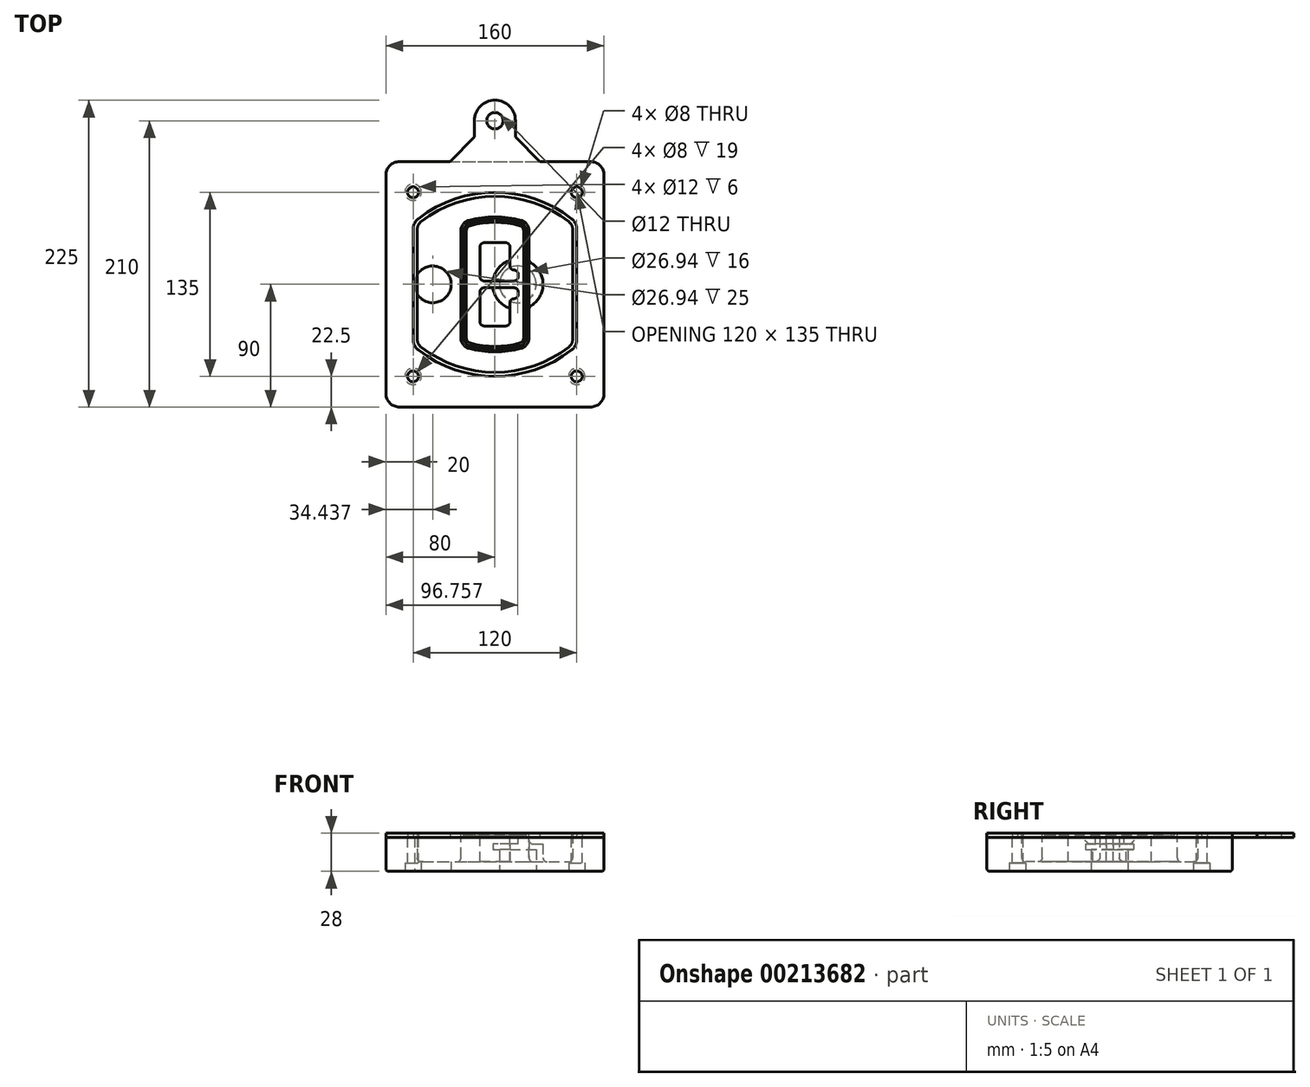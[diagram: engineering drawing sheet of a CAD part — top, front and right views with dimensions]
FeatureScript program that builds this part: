
annotation { "Feature Type Name" : "Feature", "Feature Type Description" : "" }
export const myFeature = defineFeature(function(context is Context, id is Id, definition is map)
    precondition{}
    {
        {
            var Q0;
            Q0=qCreatedBy(makeId("Top.planeOp"),FACE);
            var sketch = newSketch(context, id + "F0", { "sketchPlane" : qUnion([Q0])});
            skPoint(sketch, "E0.rect.middle", {"position": v(0, 0) * mm});
            skLineSegment(sketch, "E1.bottom", {"start": v(-70, -90) * mm, "end": v(70, -90) * mm});
            skLineSegment(sketch, "E1.top", {"start": v(-70, 90) * mm, "end": v(70, 90) * mm});
            skLineSegment(sketch, "E1.left", {"start": v(-80, -80) * mm, "end": v(-80, 80) * mm});
            skLineSegment(sketch, "E1.right", {"start": v(80, -80) * mm, "end": v(80, 80) * mm});
            skLineSegment(sketch, "E2", {"start": v(-80, 90) * mm, "end": v(80, -90) * mm, "construction": true});
            skLineSegment(sketch, "E3", {"start": v(80, 90) * mm, "end": v(-80, -90) * mm, "construction": true});
            skCircle(sketch, "E4", {"center": v(-60, 67.5) * mm, "radius": 4 * mm});
            skCircle(sketch, "E5", {"center": v(60, 67.5) * mm, "radius": 4 * mm});
            skCircle(sketch, "E6", {"center": v(60, -67.5) * mm, "radius": 4 * mm});
            skCircle(sketch, "E7", {"center": v(-60, -67.5) * mm, "radius": 4 * mm});
            skLineSegment(sketch, "E8", {"start": v(-60, 67.5) * mm, "end": v(60, 67.5) * mm, "construction": true});
            skLineSegment(sketch, "E9", {"start": v(60, 67.5) * mm, "end": v(60, -67.5) * mm, "construction": true});
            skLineSegment(sketch, "E10", {"start": v(60, -67.5) * mm, "end": v(-60, -67.5) * mm, "construction": true});
            skLineSegment(sketch, "E11", {"start": v(-60, -67.5) * mm, "end": v(-60, 67.5) * mm, "construction": true});
            skLineSegment(sketch, "E12", {"start": v(-60, 40.3) * mm, "end": v(-60, -40.3) * mm});
            skLineSegment(sketch, "E13", {"start": v(60, 40.3) * mm, "end": v(60, -40.3) * mm});
            skArc(sketch, "E14", {"start": v(56.15, 48.18) * mm, "mid": v(0, 67.5) * mm, "end": v(-56.15, 48.18) * mm});
            skArc(sketch, "E15", {"start": v(-56.15, -48.18) * mm, "mid": v(0, -67.5) * mm, "end": v(56.15, -48.18) * mm});
            skLineSegment(sketch, "E16", {"start": v(-60, 0) * mm, "end": v(60, 0) * mm, "construction": true});
            skPoint(sketch, "E17.visualSharp", {"position": v(-60, -45) * mm});
            skArc(sketch, "E17.filletArc", {"start": v(-60, -40.3) * mm, "mid": v(-58.99, -44.68) * mm, "end": v(-56.15, -48.18) * mm});
            skPoint(sketch, "E18.visualSharp", {"position": v(-60, 45) * mm});
            skArc(sketch, "E18.filletArc", {"start": v(-56.15, 48.18) * mm, "mid": v(-58.99, 44.68) * mm, "end": v(-60, 40.3) * mm});
            skPoint(sketch, "E19.visualSharp", {"position": v(60, 45) * mm});
            skArc(sketch, "E19.filletArc", {"start": v(60, 40.3) * mm, "mid": v(58.99, 44.68) * mm, "end": v(56.15, 48.18) * mm});
            skPoint(sketch, "E20.visualSharp", {"position": v(60, -45) * mm});
            skArc(sketch, "E20.filletArc", {"start": v(56.15, -48.18) * mm, "mid": v(58.99, -44.68) * mm, "end": v(60, -40.3) * mm});
            skPoint(sketch, "E21.visualSharp", {"position": v(-80, 90) * mm});
            skArc(sketch, "E21.filletArc", {"start": v(-70, 90) * mm, "mid": v(-77.07, 87.07) * mm, "end": v(-80, 80) * mm});
            skPoint(sketch, "E22.visualSharp", {"position": v(80, 90) * mm});
            skArc(sketch, "E22.filletArc", {"start": v(80, 80) * mm, "mid": v(77.07, 87.07) * mm, "end": v(70, 90) * mm});
            skPoint(sketch, "E23.visualSharp", {"position": v(80, -90) * mm});
            skArc(sketch, "E23.filletArc", {"start": v(70, -90) * mm, "mid": v(77.07, -87.07) * mm, "end": v(80, -80) * mm});
            skPoint(sketch, "E24.visualSharp", {"position": v(-80, -90) * mm});
            skArc(sketch, "E24.filletArc", {"start": v(-80, -80) * mm, "mid": v(-77.07, -87.07) * mm, "end": v(-70, -90) * mm});
            skArc(sketch, "E25.0", {"start": v(57, 40.3) * mm, "mid": v(56.3, 43.36) * mm, "end": v(54.3, 45.81) * mm});
            skLineSegment(sketch, "E25.1", {"start": v(57, 40.3) * mm, "end": v(57, -40.3) * mm});
            skArc(sketch, "E25.2", {"start": v(54.3, -45.81) * mm, "mid": v(56.3, -43.36) * mm, "end": v(57, -40.3) * mm});
            skArc(sketch, "E25.3", {"start": v(-54.3, -45.81) * mm, "mid": v(0, -64.5) * mm, "end": v(54.3, -45.81) * mm});
            skArc(sketch, "E25.4", {"start": v(-57, -40.3) * mm, "mid": v(-56.3, -43.36) * mm, "end": v(-54.3, -45.81) * mm});
            skArc(sketch, "E25.5", {"start": v(54.3, 45.81) * mm, "mid": v(0, 64.5) * mm, "end": v(-54.3, 45.81) * mm});
            skLineSegment(sketch, "E25.6", {"start": v(-57, 40.3) * mm, "end": v(-57, -40.3) * mm});
            skArc(sketch, "E25.7", {"start": v(-54.3, 45.81) * mm, "mid": v(-56.3, 43.36) * mm, "end": v(-57, 40.3) * mm});
            skArc(sketch, "E26.0", {"start": v(-58.62, 51.33) * mm, "mid": v(-62.58, 46.43) * mm, "end": v(-64, 40.3) * mm});
            skArc(sketch, "E26.1", {"start": v(58.62, 51.33) * mm, "mid": v(0, 71.5) * mm, "end": v(-58.62, 51.33) * mm});
            skArc(sketch, "E26.2", {"start": v(64, 40.3) * mm, "mid": v(62.58, 46.43) * mm, "end": v(58.62, 51.33) * mm});
            skLineSegment(sketch, "E26.3", {"start": v(64, 40.3) * mm, "end": v(64, -40.3) * mm});
            skArc(sketch, "E26.4", {"start": v(58.62, -51.33) * mm, "mid": v(62.58, -46.43) * mm, "end": v(64, -40.3) * mm});
            skLineSegment(sketch, "E26.5", {"start": v(-64, 40.3) * mm, "end": v(-64, -40.3) * mm});
            skArc(sketch, "E26.6", {"start": v(-58.62, -51.33) * mm, "mid": v(0, -71.5) * mm, "end": v(58.62, -51.33) * mm});
            skArc(sketch, "E26.7", {"start": v(-64, -40.3) * mm, "mid": v(-62.58, -46.43) * mm, "end": v(-58.62, -51.33) * mm});
            skSolve(sketch);
        }
        {
            var Q0;
            Q0=makeQuery(id+"F0.imprint","IMPRINT",FACE,{"disambiguationData":[TD([[makeQuery(id+"F0.imprint","IMPRINT",EDGE,{"derivedFrom":sQuery(id+"F0.wireOp",EDGE,"E1.bottom")}),1.0]])]});
            var Q1;
            Q1=makeQuery(id+"F0.imprint","IMPRINT",FACE,{"disambiguationData":[TD([[makeQuery(id+"F0.imprint","IMPRINT",EDGE,{"derivedFrom":sQuery(id+"F0.wireOp",EDGE,"E12")}),1.0]])]});
            var Q2;
            Q2=makeQuery(id+"F0.imprint","IMPRINT",FACE,{"disambiguationData":[TD([[makeQuery(id+"F0.imprint","IMPRINT",EDGE,{"derivedFrom":sQuery(id+"F0.wireOp",EDGE,"E25.0")}),1.0]])]});
            var Q3;
            Q3=makeQuery(id+"F0.imprint","IMPRINT",FACE,{"disambiguationData":[TD([[makeQuery(id+"F0.imprint","IMPRINT",EDGE,{"derivedFrom":sQuery(id+"F0.wireOp",EDGE,"E12")}),-1.0]])]});
            extrude(context, id + "F1", {"entities" : qUnion([Q0, Q1, Q2, Q3]), "oppositeDirection" : true, "depth" : 25 * mm});
        }
        {
            var Q0;
            Q0=makeQuery(id+"F0.imprint","IMPRINT",FACE,{"disambiguationData":[TD([[makeQuery(id+"F0.imprint","IMPRINT",EDGE,{"derivedFrom":sQuery(id+"F0.wireOp",EDGE,"E12")}),1.0]])]});
            extrude(context, id + "F2", {"entities" : qUnion([Q0]), "operationType" : NewBodyOperationType.ADD, "depth" : 3 * mm});
        }
        {
            var Q0;
            Q0=makeQuery(id+"F0.imprint","IMPRINT",FACE,{"disambiguationData":[TD([[makeQuery(id+"F0.imprint","IMPRINT",EDGE,{"derivedFrom":sQuery(id+"F0.wireOp",EDGE,"E25.0")}),1.0]])]});
            extrude(context, id + "F3", {"entities" : qUnion([Q0]), "operationType" : NewBodyOperationType.REMOVE, "oppositeDirection" : true, "depth" : 18 * mm});
        }
        {
            var Q0;
            Q0=makeQuery(id+"F2.opExtrude","CAP_FACE",FACE,{"disambiguationData":[OSD([sQuery(id+"F0.wireOp",EDGE,"E12"),sQuery(id+"F0.wireOp",EDGE,"E13"),sQuery(id+"F0.wireOp",EDGE,"E14"),sQuery(id+"F0.wireOp",EDGE,"E15"),sQuery(id+"F0.wireOp",EDGE,"E17.filletArc"),sQuery(id+"F0.wireOp",EDGE,"E18.filletArc"),sQuery(id+"F0.wireOp",EDGE,"E19.filletArc"),sQuery(id+"F0.wireOp",EDGE,"E20.filletArc"),sQuery(id+"F0.wireOp",EDGE,"E25.0"),sQuery(id+"F0.wireOp",EDGE,"E25.1"),sQuery(id+"F0.wireOp",EDGE,"E25.2"),sQuery(id+"F0.wireOp",EDGE,"E25.3"),sQuery(id+"F0.wireOp",EDGE,"E25.4"),sQuery(id+"F0.wireOp",EDGE,"E25.5"),sQuery(id+"F0.wireOp",EDGE,"E25.6"),sQuery(id+"F0.wireOp",EDGE,"E25.7")])],"isStart":false});
            var sketch = newSketch(context, id + "F4", { "sketchPlane" : qUnion([Q0])});
            skArc(sketch, "E27.0", {"start": v(-19.08, -46.97) * mm, "mid": v(0, -49.5) * mm, "end": v(19.08, -46.97) * mm});
            skArc(sketch, "E28.0", {"start": v(19.08, 46.97) * mm, "mid": v(0, 49.5) * mm, "end": v(-19.08, 46.97) * mm});
            skLineSegment(sketch, "E29", {"start": v(-25, 39.25) * mm, "end": v(-25, -39.25) * mm});
            skLineSegment(sketch, "E30", {"start": v(25, 39.25) * mm, "end": v(25, -39.25) * mm});
            skLineSegment(sketch, "E31", {"start": v(-25, 45.1) * mm, "end": v(25, 45.1) * mm, "construction": true});
            skLineSegment(sketch, "E32", {"start": v(-25, -45.1) * mm, "end": v(25, -45.1) * mm, "construction": true});
            skPoint(sketch, "E33.visualSharp", {"position": v(-25, 45.1) * mm});
            skArc(sketch, "E33.filletArc", {"start": v(-19.08, 46.97) * mm, "mid": v(-23.35, 44.11) * mm, "end": v(-25, 39.25) * mm});
            skPoint(sketch, "E34.visualSharp", {"position": v(25, 45.1) * mm});
            skArc(sketch, "E34.filletArc", {"start": v(25, 39.25) * mm, "mid": v(23.35, 44.11) * mm, "end": v(19.08, 46.97) * mm});
            skPoint(sketch, "E35.visualSharp", {"position": v(25, -45.1) * mm});
            skArc(sketch, "E35.filletArc", {"start": v(19.08, -46.97) * mm, "mid": v(23.35, -44.11) * mm, "end": v(25, -39.25) * mm});
            skPoint(sketch, "E36.visualSharp", {"position": v(-25, -45.1) * mm});
            skArc(sketch, "E36.filletArc", {"start": v(-25, -39.25) * mm, "mid": v(-23.35, -44.11) * mm, "end": v(-19.08, -46.97) * mm});
            skArc(sketch, "E37.0", {"start": v(54.3, 45.81) * mm, "mid": v(0, 64.5) * mm, "end": v(-54.3, 45.81) * mm});
            skArc(sketch, "E37.1", {"start": v(-54.3, 45.81) * mm, "mid": v(-56.3, 43.36) * mm, "end": v(-57, 40.3) * mm});
            skLineSegment(sketch, "E37.2", {"start": v(-57, 40.3) * mm, "end": v(-57, -40.3) * mm});
            skArc(sketch, "E37.3", {"start": v(-57, -40.3) * mm, "mid": v(-56.3, -43.36) * mm, "end": v(-54.3, -45.81) * mm});
            skArc(sketch, "E37.4", {"start": v(-54.3, -45.81) * mm, "mid": v(0, -64.5) * mm, "end": v(54.3, -45.81) * mm});
            skArc(sketch, "E37.5", {"start": v(54.3, -45.81) * mm, "mid": v(56.3, -43.36) * mm, "end": v(57, -40.3) * mm});
            skLineSegment(sketch, "E37.6", {"start": v(57, 40.3) * mm, "end": v(57, -40.3) * mm});
            skArc(sketch, "E37.7", {"start": v(57, 40.3) * mm, "mid": v(56.3, 43.36) * mm, "end": v(54.3, 45.81) * mm});
            skLineSegment(sketch, "E38.0", {"start": v(23, 39.25) * mm, "end": v(23, -39.25) * mm});
            skArc(sketch, "E38.1", {"start": v(18.56, -45.04) * mm, "mid": v(21.76, -42.9) * mm, "end": v(23, -39.25) * mm});
            skArc(sketch, "E38.2", {"start": v(-18.56, -45.04) * mm, "mid": v(0, -47.5) * mm, "end": v(18.56, -45.04) * mm});
            skArc(sketch, "E38.3", {"start": v(-23, -39.25) * mm, "mid": v(-21.76, -42.9) * mm, "end": v(-18.56, -45.04) * mm});
            skLineSegment(sketch, "E38.4", {"start": v(-23, 39.25) * mm, "end": v(-23, -39.25) * mm});
            skArc(sketch, "E38.5", {"start": v(23, 39.25) * mm, "mid": v(21.76, 42.9) * mm, "end": v(18.56, 45.04) * mm});
            skArc(sketch, "E38.6", {"start": v(-18.56, 45.04) * mm, "mid": v(-21.76, 42.9) * mm, "end": v(-23, 39.25) * mm});
            skArc(sketch, "E38.7", {"start": v(18.56, 45.04) * mm, "mid": v(0, 47.5) * mm, "end": v(-18.56, 45.04) * mm});
            skArc(sketch, "E39.0", {"start": v(21, 39.25) * mm, "mid": v(20.18, 41.68) * mm, "end": v(18.04, 43.1) * mm});
            skLineSegment(sketch, "E39.1", {"start": v(21, 39.25) * mm, "end": v(21, -39.25) * mm});
            skArc(sketch, "E39.2", {"start": v(18.04, -43.1) * mm, "mid": v(20.18, -41.68) * mm, "end": v(21, -39.25) * mm});
            skArc(sketch, "E39.3", {"start": v(-18.04, -43.1) * mm, "mid": v(0, -45.5) * mm, "end": v(18.04, -43.1) * mm});
            skArc(sketch, "E39.4", {"start": v(-21, -39.25) * mm, "mid": v(-20.18, -41.68) * mm, "end": v(-18.04, -43.1) * mm});
            skArc(sketch, "E39.5", {"start": v(18.04, 43.1) * mm, "mid": v(0, 45.5) * mm, "end": v(-18.04, 43.1) * mm});
            skLineSegment(sketch, "E39.6", {"start": v(-21, 39.25) * mm, "end": v(-21, -39.25) * mm});
            skArc(sketch, "E39.7", {"start": v(-18.04, 43.1) * mm, "mid": v(-20.18, 41.68) * mm, "end": v(-21, 39.25) * mm});
            skLineSegment(sketch, "E40", {"start": v(-25, 0) * mm, "end": v(25, 0) * mm, "construction": true});
            skLineSegment(sketch, "E41", {"start": v(-11, 5.5) * mm, "end": v(-11, 27.5) * mm});
            skLineSegment(sketch, "E42", {"start": v(-8, 30.5) * mm, "end": v(8, 30.5) * mm});
            skLineSegment(sketch, "E43", {"start": v(11, 27.5) * mm, "end": v(11, 13.5) * mm});
            skLineSegment(sketch, "E44", {"start": v(14, 10.5) * mm, "end": v(14, 10.5) * mm});
            skLineSegment(sketch, "E45", {"start": v(17, 7.5) * mm, "end": v(17, 5.5) * mm});
            skLineSegment(sketch, "E46", {"start": v(14, 2.5) * mm, "end": v(-8, 2.5) * mm});
            skPoint(sketch, "E47.visualSharp", {"position": v(-11, 30.5) * mm});
            skArc(sketch, "E47.filletArc", {"start": v(-8, 30.5) * mm, "mid": v(-10.12, 29.62) * mm, "end": v(-11, 27.5) * mm});
            skPoint(sketch, "E48.visualSharp", {"position": v(11, 30.5) * mm});
            skArc(sketch, "E48.filletArc", {"start": v(11, 27.5) * mm, "mid": v(10.12, 29.62) * mm, "end": v(8, 30.5) * mm});
            skPoint(sketch, "E49.visualSharp", {"position": v(11, 10.5) * mm});
            skArc(sketch, "E49.filletArc", {"start": v(11, 13.5) * mm, "mid": v(11.88, 11.38) * mm, "end": v(14, 10.5) * mm});
            skPoint(sketch, "E50.visualSharp", {"position": v(17, 10.5) * mm});
            skArc(sketch, "E50.filletArc", {"start": v(17, 7.5) * mm, "mid": v(16.12, 9.62) * mm, "end": v(14, 10.5) * mm});
            skPoint(sketch, "E51.visualSharp", {"position": v(17, 2.5) * mm});
            skArc(sketch, "E51.filletArc", {"start": v(14, 2.5) * mm, "mid": v(16.12, 3.38) * mm, "end": v(17, 5.5) * mm});
            skPoint(sketch, "E52.visualSharp", {"position": v(-11, 2.5) * mm});
            skArc(sketch, "E52.filletArc", {"start": v(-11, 5.5) * mm, "mid": v(-10.12, 3.38) * mm, "end": v(-8, 2.5) * mm});
            skLineSegment(sketch, "E53.0.MirrorCS", {"start": v(14, -2.5) * mm, "end": v(-8, -2.5) * mm});
            skArc(sketch, "E54.0.MirrorCS", {"start": v(-11, -5.5) * mm, "mid": v(-10.12, -3.38) * mm, "end": v(-8, -2.5) * mm});
            skLineSegment(sketch, "E55.0.MirrorCS", {"start": v(-11, -5.5) * mm, "end": v(-11, -27.5) * mm});
            skArc(sketch, "E56.0.MirrorCS", {"start": v(-8, -30.5) * mm, "mid": v(-10.12, -29.62) * mm, "end": v(-11, -27.5) * mm});
            skLineSegment(sketch, "E57.0.MirrorCS", {"start": v(-8, -30.5) * mm, "end": v(8, -30.5) * mm});
            skArc(sketch, "E58.0.MirrorCS", {"start": v(11, -27.5) * mm, "mid": v(10.12, -29.62) * mm, "end": v(8, -30.5) * mm});
            skLineSegment(sketch, "E59.0.MirrorCS", {"start": v(11, -27.5) * mm, "end": v(11, -13.5) * mm});
            skArc(sketch, "E60.0.MirrorCS", {"start": v(11, -13.5) * mm, "mid": v(11.88, -11.38) * mm, "end": v(14, -10.5) * mm});
            skArc(sketch, "E61.0.MirrorCS", {"start": v(17, -7.5) * mm, "mid": v(16.12, -9.62) * mm, "end": v(14, -10.5) * mm});
            skLineSegment(sketch, "E62.0.MirrorCS", {"start": v(17, -7.5) * mm, "end": v(17, -5.5) * mm});
            skArc(sketch, "E63.0.MirrorCS", {"start": v(14, -2.5) * mm, "mid": v(16.12, -3.38) * mm, "end": v(17, -5.5) * mm});
            skSolve(sketch);
        }
        {
            var Q0;
            Q0=makeQuery(id+"F4.imprint","IMPRINT",FACE,{"disambiguationData":[TD([[makeQuery(id+"F4.imprint","IMPRINT",EDGE,{"derivedFrom":sQuery(id+"F4.wireOp",EDGE,"E27.0")}),1.0]])]});
            var Q1;
            Q1=makeQuery(id+"F4.imprint","IMPRINT",FACE,{"disambiguationData":[TD([[makeQuery(id+"F4.imprint","IMPRINT",EDGE,{"derivedFrom":sQuery(id+"F4.wireOp",EDGE,"E38.0")}),-1.0]])]});
            var Q2;
            Q2=makeQuery(id+"F4.imprint","IMPRINT",FACE,{"disambiguationData":[TD([[makeQuery(id+"F4.imprint","IMPRINT",EDGE,{"derivedFrom":sQuery(id+"F4.wireOp",EDGE,"E39.0")}),1.0]])]});
            extrude(context, id + "F5", {"entities" : qUnion([Q0, Q1, Q2]), "operationType" : NewBodyOperationType.ADD, "endBound" : BoundingType.UP_TO_NEXT, "oppositeDirection" : true, "depth" : 25 * mm});
        }
        {
            var Q0;
            Q0=makeQuery(id+"F4.imprint","IMPRINT",FACE,{"disambiguationData":[TD([[makeQuery(id+"F4.imprint","IMPRINT",EDGE,{"derivedFrom":sQuery(id+"F4.wireOp",EDGE,"E38.0")}),-1.0]])]});
            extrude(context, id + "F6", {"entities" : qUnion([Q0]), "operationType" : NewBodyOperationType.REMOVE, "oppositeDirection" : true, "depth" : 2 * mm});
        }
        {
            var Q0;
            Q0=makeQuery(id+"F1.opExtrude","CAP_FACE",FACE,{"disambiguationData":[OSD([sQuery(id+"F0.wireOp",EDGE,"E1.bottom"),sQuery(id+"F0.wireOp",EDGE,"E1.top"),sQuery(id+"F0.wireOp",EDGE,"E1.left"),sQuery(id+"F0.wireOp",EDGE,"E1.right"),sQuery(id+"F0.wireOp",EDGE,"E4"),sQuery(id+"F0.wireOp",EDGE,"E5"),sQuery(id+"F0.wireOp",EDGE,"E6"),sQuery(id+"F0.wireOp",EDGE,"E7"),sQuery(id+"F0.wireOp",EDGE,"E21.filletArc"),sQuery(id+"F0.wireOp",EDGE,"E22.filletArc"),sQuery(id+"F0.wireOp",EDGE,"E23.filletArc"),sQuery(id+"F0.wireOp",EDGE,"E24.filletArc")])],"isStart":false});
            var sketch = newSketch(context, id + "F7", { "sketchPlane" : qUnion([Q0])});
            skCircle(sketch, "E64", {"center": v(16.76, 0) * mm, "radius": 13.47 * mm});
            skCircle(sketch, "E65", {"center": v(-45.56, 0) * mm, "radius": 13.47 * mm});
            skLineSegment(sketch, "E66", {"start": v(80, 0) * mm, "end": v(-80, 0) * mm});
            skCircle(sketch, "E67", {"center": v(16.76, 0) * mm, "radius": 18.47 * mm});
            skCircle(sketch, "E68", {"center": v(60, -67.5) * mm, "radius": 6 * mm});
            skCircle(sketch, "E69", {"center": v(-60, -67.5) * mm, "radius": 6 * mm});
            skCircle(sketch, "E70", {"center": v(-60, 67.5) * mm, "radius": 6 * mm});
            skCircle(sketch, "E71", {"center": v(60, 67.5) * mm, "radius": 6 * mm});
            skSolve(sketch);
        }
        {
            var Q0;
            {var subQ1=sQuery(id+"F7.wireOp",EDGE,"E66");var subQ4=sQuery(id+"F7.wireOp",EDGE,"E64");var subQ6=makeQuery(id+"F7.imprint","INTERSECT",VERTEX,{"disambiguationData":[OD(0.0)],"derivedFrom":[subQ4,subQ1]});Q0=makeQuery(id+"F7.imprint","IMPRINT",FACE,{"disambiguationData":[TD([[makeQuery(id+"F7.imprint","IMPRINT",EDGE,{"disambiguationData":[TD([[subQ6,-1.0]])],"derivedFrom":subQ4}),-1.0]])]});}
            var Q1;
            {var subQ0=sQuery(id+"F7.wireOp",EDGE,"E66");var subQ1=sQuery(id+"F7.wireOp",EDGE,"E64");var subQ3=makeQuery(id+"F7.imprint","INTERSECT",VERTEX,{"disambiguationData":[OD(0.0)],"derivedFrom":[subQ1,subQ0]});Q1=makeQuery(id+"F7.imprint","IMPRINT",FACE,{"disambiguationData":[TD([[makeQuery(id+"F7.imprint","IMPRINT",EDGE,{"disambiguationData":[TD([[subQ3,-1.0]])],"derivedFrom":subQ1}),1.0]])]});}
            var Q2;
            {var subQ0=sQuery(id+"F7.wireOp",EDGE,"E66");var subQ1=sQuery(id+"F7.wireOp",EDGE,"E64");var subQ3=makeQuery(id+"F7.imprint","INTERSECT",VERTEX,{"disambiguationData":[OD(0.0)],"derivedFrom":[subQ1,subQ0]});Q2=makeQuery(id+"F7.imprint","IMPRINT",FACE,{"disambiguationData":[TD([[makeQuery(id+"F7.imprint","IMPRINT",EDGE,{"disambiguationData":[TD([[subQ3,1.0]])],"derivedFrom":subQ1}),1.0]])]});}
            var Q3;
            {var subQ1=sQuery(id+"F7.wireOp",EDGE,"E66");var subQ4=sQuery(id+"F7.wireOp",EDGE,"E64");var subQ6=makeQuery(id+"F7.imprint","INTERSECT",VERTEX,{"disambiguationData":[OD(0.0)],"derivedFrom":[subQ4,subQ1]});Q3=makeQuery(id+"F7.imprint","IMPRINT",FACE,{"disambiguationData":[TD([[makeQuery(id+"F7.imprint","IMPRINT",EDGE,{"disambiguationData":[TD([[subQ6,1.0]])],"derivedFrom":subQ4}),-1.0]])]});}
            extrude(context, id + "F8", {"entities" : qUnion([Q0, Q1, Q2, Q3]), "operationType" : NewBodyOperationType.ADD, "oppositeDirection" : true, "depth" : 20 * mm});
        }
        {
            var Q0;
            {var subQ0=sQuery(id+"F7.wireOp",EDGE,"E66");var subQ1=sQuery(id+"F7.wireOp",EDGE,"E64");var subQ3=makeQuery(id+"F7.imprint","INTERSECT",VERTEX,{"disambiguationData":[OD(0.0)],"derivedFrom":[subQ1,subQ0]});Q0=makeQuery(id+"F7.imprint","IMPRINT",FACE,{"disambiguationData":[TD([[makeQuery(id+"F7.imprint","IMPRINT",EDGE,{"disambiguationData":[TD([[subQ3,-1.0]])],"derivedFrom":subQ1}),1.0]])]});}
            var Q1;
            {var subQ0=sQuery(id+"F7.wireOp",EDGE,"E66");var subQ1=sQuery(id+"F7.wireOp",EDGE,"E64");var subQ3=makeQuery(id+"F7.imprint","INTERSECT",VERTEX,{"disambiguationData":[OD(0.0)],"derivedFrom":[subQ1,subQ0]});Q1=makeQuery(id+"F7.imprint","IMPRINT",FACE,{"disambiguationData":[TD([[makeQuery(id+"F7.imprint","IMPRINT",EDGE,{"disambiguationData":[TD([[subQ3,1.0]])],"derivedFrom":subQ1}),1.0]])]});}
            extrude(context, id + "F9", {"entities" : qUnion([Q0, Q1]), "operationType" : NewBodyOperationType.REMOVE, "oppositeDirection" : true, "depth" : 16 * mm});
        }
        {
            var Q0;
            {var subQ0=sQuery(id+"F7.wireOp",EDGE,"E66");var subQ1=sQuery(id+"F7.wireOp",EDGE,"E65");var subQ3=makeQuery(id+"F7.imprint","INTERSECT",VERTEX,{"disambiguationData":[OD(0.0)],"derivedFrom":[subQ1,subQ0]});Q0=makeQuery(id+"F7.imprint","IMPRINT",FACE,{"disambiguationData":[TD([[makeQuery(id+"F7.imprint","IMPRINT",EDGE,{"disambiguationData":[TD([[subQ3,-1.0]])],"derivedFrom":subQ1}),1.0]])]});}
            var Q1;
            {var subQ0=sQuery(id+"F7.wireOp",EDGE,"E66");var subQ1=sQuery(id+"F7.wireOp",EDGE,"E65");var subQ3=makeQuery(id+"F7.imprint","INTERSECT",VERTEX,{"disambiguationData":[OD(0.0)],"derivedFrom":[subQ1,subQ0]});Q1=makeQuery(id+"F7.imprint","IMPRINT",FACE,{"disambiguationData":[TD([[makeQuery(id+"F7.imprint","IMPRINT",EDGE,{"disambiguationData":[TD([[subQ3,1.0]])],"derivedFrom":subQ1}),1.0]])]});}
            extrude(context, id + "F10", {"entities" : qUnion([Q0, Q1]), "operationType" : NewBodyOperationType.REMOVE, "oppositeDirection" : true, "depth" : 25 * mm});
        }
        {
            var Q0;
            Q0=makeQuery(id+"F7.imprint","IMPRINT",FACE,{"disambiguationData":[TD([[makeQuery(id+"F7.imprint","IMPRINT",EDGE,{"derivedFrom":sQuery(id+"F7.wireOp",EDGE,"E68")}),1.0]])]});
            var Q1;
            Q1=makeQuery(id+"F7.imprint","IMPRINT",FACE,{"disambiguationData":[TD([[makeQuery(id+"F7.imprint","IMPRINT",EDGE,{"derivedFrom":makeQuery(id+"F1.opExtrude","CAP_EDGE",EDGE,{"disambiguationData":[OSD([sQuery(id+"F0.wireOp",EDGE,"E5")])],"isStart":false})}),-1.0]])]});
            var Q2;
            Q2=makeQuery(id+"F7.imprint","IMPRINT",FACE,{"disambiguationData":[TD([[makeQuery(id+"F7.imprint","IMPRINT",EDGE,{"derivedFrom":sQuery(id+"F7.wireOp",EDGE,"E69")}),1.0]])]});
            var Q3;
            Q3=makeQuery(id+"F7.imprint","IMPRINT",FACE,{"disambiguationData":[TD([[makeQuery(id+"F7.imprint","IMPRINT",EDGE,{"derivedFrom":makeQuery(id+"F1.opExtrude","CAP_EDGE",EDGE,{"disambiguationData":[OSD([sQuery(id+"F0.wireOp",EDGE,"E4")])],"isStart":false})}),-1.0]])]});
            var Q4;
            Q4=makeQuery(id+"F7.imprint","IMPRINT",FACE,{"disambiguationData":[TD([[makeQuery(id+"F7.imprint","IMPRINT",EDGE,{"derivedFrom":sQuery(id+"F7.wireOp",EDGE,"E70")}),1.0]])]});
            var Q5;
            Q5=makeQuery(id+"F7.imprint","IMPRINT",FACE,{"disambiguationData":[TD([[makeQuery(id+"F7.imprint","IMPRINT",EDGE,{"derivedFrom":makeQuery(id+"F1.opExtrude","CAP_EDGE",EDGE,{"disambiguationData":[OSD([sQuery(id+"F0.wireOp",EDGE,"E7")])],"isStart":false})}),-1.0]])]});
            var Q6;
            Q6=makeQuery(id+"F7.imprint","IMPRINT",FACE,{"disambiguationData":[TD([[makeQuery(id+"F7.imprint","IMPRINT",EDGE,{"derivedFrom":sQuery(id+"F7.wireOp",EDGE,"E71")}),1.0]])]});
            var Q7;
            Q7=makeQuery(id+"F7.imprint","IMPRINT",FACE,{"disambiguationData":[TD([[makeQuery(id+"F7.imprint","IMPRINT",EDGE,{"derivedFrom":makeQuery(id+"F1.opExtrude","CAP_EDGE",EDGE,{"disambiguationData":[OSD([sQuery(id+"F0.wireOp",EDGE,"E6")])],"isStart":false})}),-1.0]])]});
            extrude(context, id + "F11", {"entities" : qUnion([Q0, Q1, Q2, Q3, Q4, Q5, Q6, Q7]), "operationType" : NewBodyOperationType.REMOVE, "oppositeDirection" : true, "depth" : 6 * mm});
        }
        {
            var Q0;
            Q0=makeQuery(id+"F9.boolean.opBoolean","COPY",FACE,{"derivedFrom":makeQuery(id+"F9.opExtrude","CAP_FACE",FACE,{"disambiguationData":[OSD([sQuery(id+"F7.wireOp",EDGE,"E64")])],"isStart":false})});
            var sketch = newSketch(context, id + "F12", { "sketchPlane" : qUnion([Q0])});
            skArc(sketch, "E72.0", {"start": v(11, 17.55) * mm, "mid": v(2.57, 11.82) * mm, "end": v(-1.54, 2.5) * mm});
            skArc(sketch, "E72.1", {"start": v(-1.54, -2.5) * mm, "mid": v(2.57, -11.82) * mm, "end": v(11, -17.55) * mm});
            skLineSegment(sketch, "E73", {"start": v(-1.54, -2.5) * mm, "end": v(14, -2.5) * mm});
            skLineSegment(sketch, "E74.0", {"start": v(14, 2.5) * mm, "end": v(-1.54, 2.5) * mm});
            skArc(sketch, "E74.1", {"start": v(14, 2.5) * mm, "mid": v(16.12, 3.38) * mm, "end": v(17, 5.5) * mm});
            skLineSegment(sketch, "E74.2", {"start": v(17, 7.5) * mm, "end": v(17, 5.5) * mm});
            skArc(sketch, "E74.3", {"start": v(17, 7.5) * mm, "mid": v(16.12, 9.62) * mm, "end": v(14, 10.5) * mm});
            skArc(sketch, "E74.4", {"start": v(11, 13.5) * mm, "mid": v(11.88, 11.38) * mm, "end": v(14, 10.5) * mm});
            skLineSegment(sketch, "E74.5", {"start": v(11, 17.55) * mm, "end": v(11, 13.5) * mm});
            skLineSegment(sketch, "E74.7", {"start": v(14, -2.5) * mm, "end": v(-1.54, -2.5) * mm});
            skArc(sketch, "E74.8", {"start": v(14, -2.5) * mm, "mid": v(16.12, -3.38) * mm, "end": v(17, -5.5) * mm});
            skLineSegment(sketch, "E74.9", {"start": v(17, -7.5) * mm, "end": v(17, -5.5) * mm});
            skArc(sketch, "E74.10", {"start": v(17, -7.5) * mm, "mid": v(16.12, -9.62) * mm, "end": v(14, -10.5) * mm});
            skArc(sketch, "E74.11", {"start": v(11, -13.5) * mm, "mid": v(11.88, -11.38) * mm, "end": v(14, -10.5) * mm});
            skLineSegment(sketch, "E74.12", {"start": v(11, -17.55) * mm, "end": v(11, -13.5) * mm});
            skPoint(sketch, "E75.orphan", {"position": v(11, -27.5) * mm});
            skPoint(sketch, "E76.orphan", {"position": v(-8, -2.5) * mm});
            skPoint(sketch, "E77.orphan", {"position": v(-8, 2.5) * mm});
            skPoint(sketch, "E78.orphan", {"position": v(11, 27.5) * mm});
            skSolve(sketch);
        }
        {
            var Q0;
            {var subQ7=sQuery(id+"F12.wireOp",EDGE,"E72.0");var subQ14=sQuery(id+"F12.wireOp",EDGE,"E72.1");var subQ16=sQuery(id+"F12.wireOp",EDGE,"E74.1");var subQ18=sQuery(id+"F12.wireOp",EDGE,"E74.8");Q0=qUnion([makeQuery(id+"F12.imprint","IMPRINT",FACE,{"disambiguationData":[TD([[makeQuery(id+"F12.imprint","IMPRINT",EDGE,{"derivedFrom":subQ7}),1.0]])]}),makeQuery(id+"F12.imprint","IMPRINT",FACE,{"disambiguationData":[TD([[makeQuery(id+"F12.imprint","IMPRINT",EDGE,{"derivedFrom":subQ14}),1.0]])]}),makeQuery(id+"F12.imprint","IMPRINT",FACE,{"disambiguationData":[TD([[makeQuery(id+"F12.imprint","IMPRINT",EDGE,{"derivedFrom":subQ16}),1.0]])]}),makeQuery(id+"F12.imprint","IMPRINT",FACE,{"disambiguationData":[TD([[makeQuery(id+"F12.imprint","IMPRINT",EDGE,{"derivedFrom":subQ18}),-1.0]])]})]);}
            var Q1;
            Q1=makeQuery(id+"F5.boolean.opBoolean","SPLIT",FACE,{"disambiguationData":[TD([makeQuery(id+"F5.opExtrude","SWEPT_FACE",FACE,{"disambiguationData":[OSD([sQuery(id+"F4.wireOp",EDGE,"E41")])]})])],"derivedFrom":makeQuery(id+"F3.boolean.opBoolean","COPY",FACE,{"derivedFrom":makeQuery(id+"F3.opExtrude","CAP_FACE",FACE,{"disambiguationData":[OSD([sQuery(id+"F0.wireOp",EDGE,"E25.0"),sQuery(id+"F0.wireOp",EDGE,"E25.1"),sQuery(id+"F0.wireOp",EDGE,"E25.2"),sQuery(id+"F0.wireOp",EDGE,"E25.3"),sQuery(id+"F0.wireOp",EDGE,"E25.4"),sQuery(id+"F0.wireOp",EDGE,"E25.5"),sQuery(id+"F0.wireOp",EDGE,"E25.6"),sQuery(id+"F0.wireOp",EDGE,"E25.7")])],"isStart":false})})});
            extrude(context, id + "F13", {"entities" : qUnion([Q0]), "operationType" : NewBodyOperationType.REMOVE, "endBound" : BoundingType.UP_TO_SURFACE, "endBoundEntityFace" : qUnion([Q1]), "depth" : 25 * mm});
        }
        {
            var Q0;
            Q0=makeQuery(id+"F3.boolean.opBoolean","COPY",EDGE,{"derivedFrom":makeQuery(id+"F3.opExtrude","CAP_EDGE",EDGE,{"disambiguationData":[OSD([sQuery(id+"F0.wireOp",EDGE,"E25.6")])],"isStart":false})});
            var Q1;
            Q1=makeQuery(id+"F8.boolean.opBoolean","INTERSECT",EDGE,{"derivedFrom":[makeQuery(id+"F5.opExtrude","SWEPT_FACE",FACE,{"disambiguationData":[OSD([sQuery(id+"F4.wireOp",EDGE,"E30")])]}),makeQuery(id+"F8.opExtrude","CAP_FACE",FACE,{"disambiguationData":[OSD([sQuery(id+"F7.wireOp",EDGE,"E67")])],"isStart":false})]});
            var Q2;
            Q2=makeQuery(id+"F8.boolean.opBoolean","INTERSECT",EDGE,{"disambiguationData":[OD(1.0)],"derivedFrom":[makeQuery(id+"F5.opExtrude","SWEPT_FACE",FACE,{"disambiguationData":[OSD([sQuery(id+"F4.wireOp",EDGE,"E30")])]}),makeQuery(id+"F8.opExtrude","SWEPT_FACE",FACE,{"disambiguationData":[OSD([sQuery(id+"F7.wireOp",EDGE,"E67")])]})]});
            var Q3;
            {var subQ0=sQuery(id+"F4.wireOp",EDGE,"E30");Q3=makeQuery(id+"F8.boolean.opBoolean","SPLIT",EDGE,{"disambiguationData":[TD([makeQuery(id+"F5.opExtrude","SWEPT_FACE",FACE,{"disambiguationData":[OSD([sQuery(id+"F4.wireOp",EDGE,"E35.filletArc")])]})])],"derivedFrom":makeQuery(id+"F5.opExtrude","CAP_EDGE",EDGE,{"disambiguationData":[OSD([subQ0])],"isStart":false})});}
            var Q4;
            {var subQ0=sQuery(id+"F0.wireOp",EDGE,"E25.7");var subQ1=sQuery(id+"F0.wireOp",EDGE,"E25.1");var subQ2=sQuery(id+"F0.wireOp",EDGE,"E25.6");var subQ3=sQuery(id+"F0.wireOp",EDGE,"E25.5");var subQ4=sQuery(id+"F0.wireOp",EDGE,"E25.4");var subQ5=sQuery(id+"F0.wireOp",EDGE,"E25.0");var subQ6=sQuery(id+"F0.wireOp",EDGE,"E25.2");var subQ7=sQuery(id+"F0.wireOp",EDGE,"E25.3");Q4=makeQuery(id+"F8.boolean.opBoolean","INTERSECT",EDGE,{"derivedFrom":[makeQuery(id+"F5.boolean.opBoolean","SPLIT",FACE,{"disambiguationData":[TD([makeQuery(id+"F2.opExtrude","SWEPT_FACE",FACE,{"disambiguationData":[OSD([subQ5])]})])],"derivedFrom":makeQuery(id+"F3.boolean.opBoolean","COPY",FACE,{"derivedFrom":makeQuery(id+"F3.opExtrude","CAP_FACE",FACE,{"disambiguationData":[OSD([subQ5,subQ1,subQ6,subQ7,subQ4,subQ3,subQ2,subQ0])],"isStart":false})})}),makeQuery(id+"F8.opExtrude","SWEPT_FACE",FACE,{"disambiguationData":[OSD([sQuery(id+"F7.wireOp",EDGE,"E67")])]})]});}
            var Q5;
            Q5=makeQuery(id+"F8.boolean.opBoolean","INTERSECT",EDGE,{"disambiguationData":[OD(0.0)],"derivedFrom":[makeQuery(id+"F5.opExtrude","SWEPT_FACE",FACE,{"disambiguationData":[OSD([sQuery(id+"F4.wireOp",EDGE,"E30")])]}),makeQuery(id+"F8.opExtrude","SWEPT_FACE",FACE,{"disambiguationData":[OSD([sQuery(id+"F7.wireOp",EDGE,"E67")])]})]});
            fillet(context, id + "F14", {"entities" : qUnion([Q0, Q1, Q2, Q3, Q4, Q5]), "radius" : 3 * mm, "tangentPropagation" : true, "allowEdgeOverflow" : false});
        }
        {
            var Q0;
            Q0=makeQuery(id+"F1.opExtrude","CAP_EDGE",EDGE,{"disambiguationData":[OSD([sQuery(id+"F0.wireOp",EDGE,"E1.bottom")])],"isStart":false});
            fillet(context, id + "F15", {"entities" : qUnion([Q0]), "radius" : 2 * mm, "tangentPropagation" : true, "allowEdgeOverflow" : false});
        }
        {
            var Q0;
            Q0=qCreatedBy(makeId("Top.planeOp"),FACE);
            var sketch = newSketch(context, id + "F16", { "sketchPlane" : qUnion([Q0])});
            skArc(sketch, "E79.0", {"start": v(56.15, 48.18) * mm, "mid": v(0, 67.5) * mm, "end": v(-56.15, 48.18) * mm});
            skArc(sketch, "E79.1", {"start": v(-56.15, 48.18) * mm, "mid": v(-58.99, 44.68) * mm, "end": v(-60, 40.3) * mm});
            skLineSegment(sketch, "E79.2", {"start": v(-60, 40.3) * mm, "end": v(-60, -40.3) * mm});
            skArc(sketch, "E79.3", {"start": v(-60, -40.3) * mm, "mid": v(-58.99, -44.68) * mm, "end": v(-56.15, -48.18) * mm});
            skArc(sketch, "E79.4", {"start": v(-56.15, -48.18) * mm, "mid": v(0, -67.5) * mm, "end": v(56.15, -48.18) * mm});
            skArc(sketch, "E79.5", {"start": v(56.15, -48.18) * mm, "mid": v(58.99, -44.68) * mm, "end": v(60, -40.3) * mm});
            skLineSegment(sketch, "E79.6", {"start": v(60, 40.3) * mm, "end": v(60, -40.3) * mm});
            skArc(sketch, "E79.7", {"start": v(60, 40.3) * mm, "mid": v(58.99, 44.68) * mm, "end": v(56.15, 48.18) * mm});
            skLineSegment(sketch, "E79.8", {"start": v(-70, 90) * mm, "end": v(70, 90) * mm});
            skArc(sketch, "E79.9", {"start": v(80, 80) * mm, "mid": v(77.07, 87.07) * mm, "end": v(70, 90) * mm});
            skLineSegment(sketch, "E79.10", {"start": v(80, -80) * mm, "end": v(80, 80) * mm});
            skArc(sketch, "E79.11", {"start": v(70, -90) * mm, "mid": v(77.07, -87.07) * mm, "end": v(80, -80) * mm});
            skLineSegment(sketch, "E79.12", {"start": v(-70, -90) * mm, "end": v(70, -90) * mm});
            skArc(sketch, "E79.13", {"start": v(-80, -80) * mm, "mid": v(-77.07, -87.07) * mm, "end": v(-70, -90) * mm});
            skLineSegment(sketch, "E79.14", {"start": v(-80, -80) * mm, "end": v(-80, 80) * mm});
            skArc(sketch, "E79.15", {"start": v(-70, 90) * mm, "mid": v(-77.07, 87.07) * mm, "end": v(-80, 80) * mm});
            skCircle(sketch, "E79.16", {"center": v(-60, 67.5) * mm, "radius": 4 * mm});
            skCircle(sketch, "E79.17", {"center": v(60, 67.5) * mm, "radius": 4 * mm});
            skCircle(sketch, "E79.18", {"center": v(60, -67.5) * mm, "radius": 4 * mm});
            skCircle(sketch, "E79.19", {"center": v(-60, -67.5) * mm, "radius": 4 * mm});
            skLineSegment(sketch, "E80", {"start": v(0, 90) * mm, "end": v(0, 120) * mm, "construction": true});
            skPoint(sketch, "E80.endSnap0", {"position": v(0, 90) * mm});
            skCircle(sketch, "E81", {"center": v(0, 120) * mm, "radius": 6 * mm});
            skArc(sketch, "E82", {"start": v(15, 120) * mm, "mid": v(0, 135) * mm, "end": v(-15, 120) * mm});
            skLineSegment(sketch, "E83", {"start": v(-15, 120) * mm, "end": v(-15, 108) * mm});
            skLineSegment(sketch, "E84", {"start": v(15, 120) * mm, "end": v(15, 108) * mm});
            skLineSegment(sketch, "E85", {"start": v(15, 108) * mm, "end": v(33, 90) * mm});
            skLineSegment(sketch, "E86", {"start": v(-15, 108) * mm, "end": v(-33, 90) * mm});
            skLineSegment(sketch, "E87", {"start": v(-80, 0) * mm, "end": v(80, 0) * mm});
            skArc(sketch, "E88.MirrorCS", {"start": v(15, -120) * mm, "mid": v(0, -135) * mm, "end": v(-15, -120) * mm});
            skCircle(sketch, "E89.MirrorC", {"center": v(0, -120) * mm, "radius": 6 * mm});
            skLineSegment(sketch, "E90.MirrorCS", {"start": v(15, -120) * mm, "end": v(15, -108) * mm});
            skLineSegment(sketch, "E91.MirrorCS", {"start": v(-15, -120) * mm, "end": v(-15, -108) * mm});
            skLineSegment(sketch, "E92.MirrorCS", {"start": v(0, -90) * mm, "end": v(0, -120) * mm, "construction": true});
            skLineSegment(sketch, "E93.MirrorCS", {"start": v(-15, -108) * mm, "end": v(-33, -90) * mm});
            skLineSegment(sketch, "E94.MirrorCS", {"start": v(15, -108) * mm, "end": v(33, -90) * mm});
            skSolve(sketch);
        }
        {
            var Q0;
            Q0=makeQuery(id+"F16.imprint","IMPRINT",FACE,{"disambiguationData":[TD([[makeQuery(id+"F16.imprint","IMPRINT",EDGE,{"derivedFrom":sQuery(id+"F16.wireOp",EDGE,"E81")}),-1.0]])]});
            var Q1;
            Q1=makeQuery(id+"F16.imprint","IMPRINT",FACE,{"disambiguationData":[TD([[makeQuery(id+"F16.imprint","IMPRINT",EDGE,{"derivedFrom":sQuery(id+"F16.wireOp",EDGE,"E79.0")}),-1.0]])]});
            var Q2;
            {var subQ13=sQuery(id+"F16.wireOp",EDGE,"E79.3");Q2=makeQuery(id+"F16.imprint","IMPRINT",FACE,{"disambiguationData":[TD([[makeQuery(id+"F16.imprint","IMPRINT",EDGE,{"derivedFrom":subQ13}),-1.0]])]});}
            var Q3;
            Q3=makeQuery(id+"F16.imprint","IMPRINT",FACE,{"disambiguationData":[TD([[makeQuery(id+"F16.imprint","IMPRINT",EDGE,{"derivedFrom":sQuery(id+"F16.wireOp",EDGE,"E88.MirrorCS")}),-1.0]])]});
            var Q4;
            Q4=makeQuery(id+"F2.opExtrude","CAP_FACE",FACE,{"disambiguationData":[OSD([sQuery(id+"F0.wireOp",EDGE,"E12"),sQuery(id+"F0.wireOp",EDGE,"E13"),sQuery(id+"F0.wireOp",EDGE,"E14"),sQuery(id+"F0.wireOp",EDGE,"E15"),sQuery(id+"F0.wireOp",EDGE,"E17.filletArc"),sQuery(id+"F0.wireOp",EDGE,"E18.filletArc"),sQuery(id+"F0.wireOp",EDGE,"E19.filletArc"),sQuery(id+"F0.wireOp",EDGE,"E20.filletArc"),sQuery(id+"F0.wireOp",EDGE,"E25.0"),sQuery(id+"F0.wireOp",EDGE,"E25.1"),sQuery(id+"F0.wireOp",EDGE,"E25.2"),sQuery(id+"F0.wireOp",EDGE,"E25.3"),sQuery(id+"F0.wireOp",EDGE,"E25.4"),sQuery(id+"F0.wireOp",EDGE,"E25.5"),sQuery(id+"F0.wireOp",EDGE,"E25.6"),sQuery(id+"F0.wireOp",EDGE,"E25.7")])],"isStart":false});
            extrude(context, id + "F17", {"entities" : qUnion([Q0, Q1, Q2, Q3]), "endBound" : BoundingType.UP_TO_SURFACE, "endBoundEntityFace" : qUnion([Q4]), "depth" : 0.12 * mm});
        }
    });
